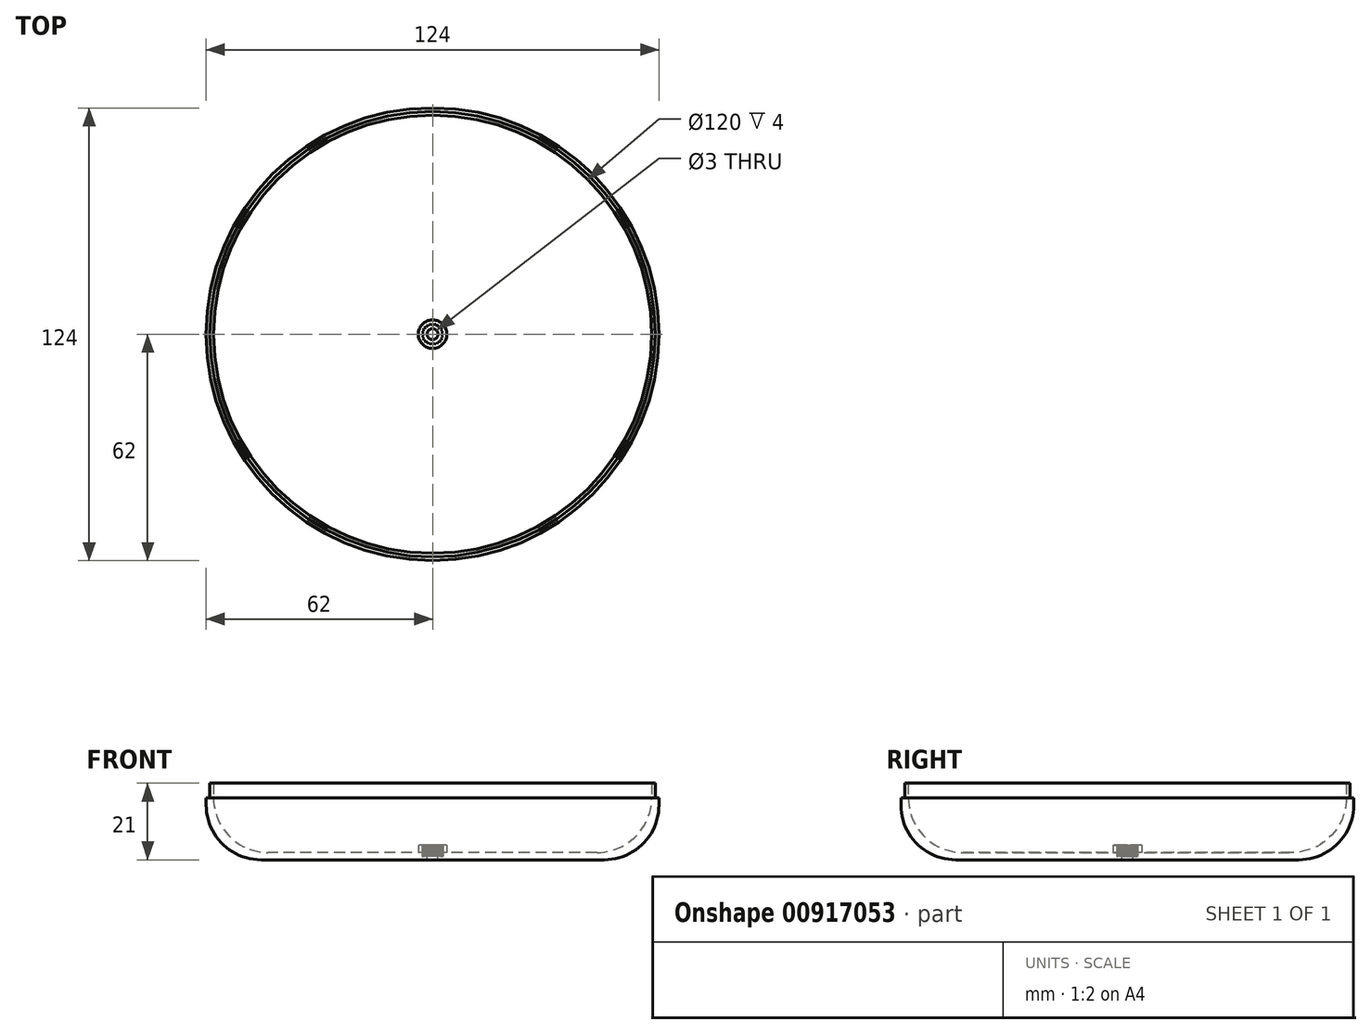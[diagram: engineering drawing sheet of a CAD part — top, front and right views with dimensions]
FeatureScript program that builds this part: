
annotation { "Feature Type Name" : "Feature", "Feature Type Description" : "" }
export const myFeature = defineFeature(function(context is Context, id is Id, definition is map)
    precondition{}
    {
        {
            var Q0;
            Q0=qCreatedBy(makeId("Top.planeOp"),FACE);
            var sketch = newSketch(context, id + "F0", { "sketchPlane" : qUnion([Q0])});
            skCircle(sketch, "E0", {"center": v(0, 0) * mm, "radius": 62 * mm});
            skSolve(sketch);
        }
        {
            var Q0;
            Q0=makeQuery(id+"F0.imprint","IMPRINT",FACE,{"disambiguationData":[TD([[makeQuery(id+"F0.imprint","IMPRINT",EDGE,{"derivedFrom":sQuery(id+"F0.wireOp",EDGE,"E0")}),1.0]])]});
            extrude(context, id + "F1", {"entities" : qUnion([Q0]), "oppositeDirection" : true, "depth" : 17 * mm, "offsetDistance" : 25 * mm});
        }
        {
            var Q0;
            Q0=makeQuery(id+"F1.opExtrude","CAP_FACE",FACE,{"disambiguationData":[OSD([sQuery(id+"F0.wireOp",EDGE,"E0")])],"isStart":true});
            var sketch = newSketch(context, id + "F2", { "sketchPlane" : qUnion([Q0])});
            skCircle(sketch, "E1", {"center": v(0, 0) * mm, "radius": 60 * mm});
            skSolve(sketch);
        }
        {
            var Q0;
            Q0=makeQuery(id+"F2.imprint","IMPRINT",FACE,{"disambiguationData":[TD([[makeQuery(id+"F2.imprint","IMPRINT",EDGE,{"derivedFrom":sQuery(id+"F2.wireOp",EDGE,"E1")}),1.0]])]});
            extrude(context, id + "F3", {"entities" : qUnion([Q0]), "operationType" : NewBodyOperationType.REMOVE, "oppositeDirection" : true, "depth" : 15 * mm, "offsetDistance" : 25 * mm});
        }
        {
            var Q0;
            Q0=makeQuery(id+"F3.boolean.opBoolean","COPY",EDGE,{"derivedFrom":makeQuery(id+"F3.opExtrude","CAP_EDGE",EDGE,{"disambiguationData":[OSD([sQuery(id+"F2.wireOp",EDGE,"E1")])],"isStart":false})});
            var Q1;
            Q1=makeQuery(id+"F1.opExtrude","CAP_EDGE",EDGE,{"disambiguationData":[OSD([sQuery(id+"F0.wireOp",EDGE,"E0")])],"isStart":false});
            fillet(context, id + "F4", {"entities" : qUnion([Q0, Q1]), "radius" : 15 * mm, "tangentPropagation" : true, "allowEdgeOverflow" : false});
        }
        {
            var Q0;
            Q0=makeQuery(id+"F1.opExtrude","CAP_FACE",FACE,{"disambiguationData":[OSD([sQuery(id+"F0.wireOp",EDGE,"E0")])],"isStart":true});
            var sketch = newSketch(context, id + "F5", { "sketchPlane" : qUnion([Q0])});
            skCircle(sketch, "E2", {"center": v(0, 0) * mm, "radius": 61 * mm});
            skSolve(sketch);
        }
        {
            var Q0;
            Q0=makeQuery(id+"F5.imprint","IMPRINT",FACE,{"disambiguationData":[TD([[makeQuery(id+"F5.imprint","IMPRINT",EDGE,{"derivedFrom":sQuery(id+"F5.wireOp",EDGE,"E2")}),1.0]])]});
            extrude(context, id + "F6", {"entities" : qUnion([Q0]), "operationType" : NewBodyOperationType.ADD, "depth" : 4 * mm, "offsetDistance" : 25 * mm});
        }
        {
            var Q0;
            Q0=makeQuery(id+"F3.boolean.opBoolean","COPY",FACE,{"derivedFrom":makeQuery(id+"F3.opExtrude","CAP_FACE",FACE,{"disambiguationData":[OSD([sQuery(id+"F2.wireOp",EDGE,"E1")])],"isStart":false})});
            var sketch = newSketch(context, id + "F7", { "sketchPlane" : qUnion([Q0])});
            skCircle(sketch, "E3", {"center": v(0, 0) * mm, "radius": 2.56 * mm});
            skPoint(sketch, "E4", {"position": v(2.56, 0) * mm});
            skPoint(sketch, "E5.1.0", {"position": v(2.47, 0.66) * mm});
            skCircle(sketch, "E6", {"center": v(0, 0) * mm, "radius": 2.9 * mm});
            skPoint(sketch, "E7", {"position": v(2.88, 0.38) * mm});
            skLineSegment(sketch, "E8", {"start": v(0, 0) * mm, "end": v(2.47, 0.66) * mm});
            skLineSegment(sketch, "E9", {"start": v(0, 0) * mm, "end": v(2.56, 0) * mm});
            skLineSegment(sketch, "E10", {"start": v(0, 0) * mm, "end": v(2.88, 0.38) * mm});
            skLineSegment(sketch, "E11", {"start": v(2.47, 0.66) * mm, "end": v(2.88, 0.38) * mm});
            skLineSegment(sketch, "E12", {"start": v(2.88, 0.38) * mm, "end": v(2.56, 0) * mm});
            skPoint(sketch, "E13.1.0", {"position": v(2.22, 1.28) * mm});
            skLineSegment(sketch, "E13.1.2", {"start": v(2.22, 1.28) * mm, "end": v(2.68, 1.1) * mm});
            skLineSegment(sketch, "E13.1.3", {"start": v(2.68, 1.1) * mm, "end": v(2.47, 0.66) * mm});
            skPoint(sketch, "E13.1.4", {"position": v(2.68, 1.1) * mm});
            skPoint(sketch, "E13.2.0", {"position": v(1.81, 1.81) * mm});
            skPoint(sketch, "E13.2.1", {"position": v(2.22, 1.28) * mm});
            skLineSegment(sketch, "E13.2.2", {"start": v(1.81, 1.81) * mm, "end": v(2.3, 1.77) * mm});
            skLineSegment(sketch, "E13.2.3", {"start": v(2.3, 1.77) * mm, "end": v(2.22, 1.28) * mm});
            skPoint(sketch, "E13.2.4", {"position": v(2.3, 1.77) * mm});
            skPoint(sketch, "E13.3.0", {"position": v(1.28, 2.22) * mm});
            skPoint(sketch, "E13.3.1", {"position": v(1.81, 1.81) * mm});
            skLineSegment(sketch, "E13.3.2", {"start": v(1.28, 2.22) * mm, "end": v(1.77, 2.3) * mm});
            skLineSegment(sketch, "E13.3.3", {"start": v(1.77, 2.3) * mm, "end": v(1.81, 1.81) * mm});
            skPoint(sketch, "E13.3.4", {"position": v(1.77, 2.3) * mm});
            skPoint(sketch, "E13.4.0", {"position": v(0.66, 2.47) * mm});
            skPoint(sketch, "E13.4.1", {"position": v(1.28, 2.22) * mm});
            skLineSegment(sketch, "E13.4.2", {"start": v(0.66, 2.47) * mm, "end": v(1.1, 2.68) * mm});
            skLineSegment(sketch, "E13.4.3", {"start": v(1.1, 2.68) * mm, "end": v(1.28, 2.22) * mm});
            skPoint(sketch, "E13.4.4", {"position": v(1.1, 2.68) * mm});
            skPoint(sketch, "E13.5.0", {"position": v(0, 2.56) * mm});
            skPoint(sketch, "E13.5.1", {"position": v(0.66, 2.47) * mm});
            skLineSegment(sketch, "E13.5.2", {"start": v(0, 2.56) * mm, "end": v(0.38, 2.88) * mm});
            skLineSegment(sketch, "E13.5.3", {"start": v(0.38, 2.88) * mm, "end": v(0.66, 2.47) * mm});
            skPoint(sketch, "E13.5.4", {"position": v(0.38, 2.88) * mm});
            skPoint(sketch, "E13.6.0", {"position": v(-0.66, 2.47) * mm});
            skPoint(sketch, "E13.6.1", {"position": v(0, 2.56) * mm});
            skLineSegment(sketch, "E13.6.2", {"start": v(-0.66, 2.47) * mm, "end": v(-0.38, 2.88) * mm});
            skLineSegment(sketch, "E13.6.3", {"start": v(-0.38, 2.88) * mm, "end": v(0, 2.56) * mm});
            skPoint(sketch, "E13.6.4", {"position": v(-0.38, 2.88) * mm});
            skPoint(sketch, "E13.7.0", {"position": v(-1.28, 2.22) * mm});
            skPoint(sketch, "E13.7.1", {"position": v(-0.66, 2.47) * mm});
            skLineSegment(sketch, "E13.7.2", {"start": v(-1.28, 2.22) * mm, "end": v(-1.1, 2.68) * mm});
            skLineSegment(sketch, "E13.7.3", {"start": v(-1.1, 2.68) * mm, "end": v(-0.66, 2.47) * mm});
            skPoint(sketch, "E13.7.4", {"position": v(-1.1, 2.68) * mm});
            skPoint(sketch, "E13.8.0", {"position": v(-1.81, 1.81) * mm});
            skPoint(sketch, "E13.8.1", {"position": v(-1.28, 2.22) * mm});
            skLineSegment(sketch, "E13.8.2", {"start": v(-1.81, 1.81) * mm, "end": v(-1.77, 2.3) * mm});
            skLineSegment(sketch, "E13.8.3", {"start": v(-1.77, 2.3) * mm, "end": v(-1.28, 2.22) * mm});
            skPoint(sketch, "E13.8.4", {"position": v(-1.77, 2.3) * mm});
            skPoint(sketch, "E13.9.0", {"position": v(-2.22, 1.28) * mm});
            skPoint(sketch, "E13.9.1", {"position": v(-1.81, 1.81) * mm});
            skLineSegment(sketch, "E13.9.2", {"start": v(-2.22, 1.28) * mm, "end": v(-2.3, 1.77) * mm});
            skLineSegment(sketch, "E13.9.3", {"start": v(-2.3, 1.77) * mm, "end": v(-1.81, 1.81) * mm});
            skPoint(sketch, "E13.9.4", {"position": v(-2.3, 1.77) * mm});
            skPoint(sketch, "E13.10.0", {"position": v(-2.47, 0.66) * mm});
            skPoint(sketch, "E13.10.1", {"position": v(-2.22, 1.28) * mm});
            skLineSegment(sketch, "E13.10.2", {"start": v(-2.47, 0.66) * mm, "end": v(-2.68, 1.1) * mm});
            skLineSegment(sketch, "E13.10.3", {"start": v(-2.68, 1.1) * mm, "end": v(-2.22, 1.28) * mm});
            skPoint(sketch, "E13.10.4", {"position": v(-2.68, 1.1) * mm});
            skPoint(sketch, "E13.11.0", {"position": v(-2.56, 0) * mm});
            skPoint(sketch, "E13.11.1", {"position": v(-2.47, 0.66) * mm});
            skLineSegment(sketch, "E13.11.2", {"start": v(-2.56, 0) * mm, "end": v(-2.88, 0.38) * mm});
            skLineSegment(sketch, "E13.11.3", {"start": v(-2.88, 0.38) * mm, "end": v(-2.47, 0.66) * mm});
            skPoint(sketch, "E13.11.4", {"position": v(-2.88, 0.38) * mm});
            skPoint(sketch, "E13.12.0", {"position": v(-2.47, -0.66) * mm});
            skPoint(sketch, "E13.12.1", {"position": v(-2.56, 0) * mm});
            skLineSegment(sketch, "E13.12.2", {"start": v(-2.47, -0.66) * mm, "end": v(-2.88, -0.38) * mm});
            skLineSegment(sketch, "E13.12.3", {"start": v(-2.88, -0.38) * mm, "end": v(-2.56, 0) * mm});
            skPoint(sketch, "E13.12.4", {"position": v(-2.88, -0.38) * mm});
            skPoint(sketch, "E13.13.0", {"position": v(-2.22, -1.28) * mm});
            skPoint(sketch, "E13.13.1", {"position": v(-2.47, -0.66) * mm});
            skLineSegment(sketch, "E13.13.2", {"start": v(-2.22, -1.28) * mm, "end": v(-2.68, -1.1) * mm});
            skLineSegment(sketch, "E13.13.3", {"start": v(-2.68, -1.1) * mm, "end": v(-2.47, -0.66) * mm});
            skPoint(sketch, "E13.13.4", {"position": v(-2.68, -1.1) * mm});
            skPoint(sketch, "E13.14.0", {"position": v(-1.81, -1.81) * mm});
            skPoint(sketch, "E13.14.1", {"position": v(-2.22, -1.28) * mm});
            skLineSegment(sketch, "E13.14.2", {"start": v(-1.81, -1.81) * mm, "end": v(-2.3, -1.77) * mm});
            skLineSegment(sketch, "E13.14.3", {"start": v(-2.3, -1.77) * mm, "end": v(-2.22, -1.28) * mm});
            skPoint(sketch, "E13.14.4", {"position": v(-2.3, -1.77) * mm});
            skPoint(sketch, "E13.15.0", {"position": v(-1.28, -2.22) * mm});
            skPoint(sketch, "E13.15.1", {"position": v(-1.81, -1.81) * mm});
            skLineSegment(sketch, "E13.15.2", {"start": v(-1.28, -2.22) * mm, "end": v(-1.77, -2.3) * mm});
            skLineSegment(sketch, "E13.15.3", {"start": v(-1.77, -2.3) * mm, "end": v(-1.81, -1.81) * mm});
            skPoint(sketch, "E13.15.4", {"position": v(-1.77, -2.3) * mm});
            skPoint(sketch, "E13.16.0", {"position": v(-0.66, -2.47) * mm});
            skPoint(sketch, "E13.16.1", {"position": v(-1.28, -2.22) * mm});
            skLineSegment(sketch, "E13.16.2", {"start": v(-0.66, -2.47) * mm, "end": v(-1.1, -2.68) * mm});
            skLineSegment(sketch, "E13.16.3", {"start": v(-1.1, -2.68) * mm, "end": v(-1.28, -2.22) * mm});
            skPoint(sketch, "E13.16.4", {"position": v(-1.1, -2.68) * mm});
            skPoint(sketch, "E13.17.0", {"position": v(0, -2.56) * mm});
            skPoint(sketch, "E13.17.1", {"position": v(-0.66, -2.47) * mm});
            skLineSegment(sketch, "E13.17.2", {"start": v(0, -2.56) * mm, "end": v(-0.38, -2.88) * mm});
            skLineSegment(sketch, "E13.17.3", {"start": v(-0.38, -2.88) * mm, "end": v(-0.66, -2.47) * mm});
            skPoint(sketch, "E13.17.4", {"position": v(-0.38, -2.88) * mm});
            skPoint(sketch, "E13.18.0", {"position": v(0.66, -2.47) * mm});
            skPoint(sketch, "E13.18.1", {"position": v(0, -2.56) * mm});
            skLineSegment(sketch, "E13.18.2", {"start": v(0.66, -2.47) * mm, "end": v(0.38, -2.88) * mm});
            skLineSegment(sketch, "E13.18.3", {"start": v(0.38, -2.88) * mm, "end": v(0, -2.56) * mm});
            skPoint(sketch, "E13.18.4", {"position": v(0.38, -2.88) * mm});
            skPoint(sketch, "E13.19.0", {"position": v(1.28, -2.22) * mm});
            skPoint(sketch, "E13.19.1", {"position": v(0.66, -2.47) * mm});
            skLineSegment(sketch, "E13.19.2", {"start": v(1.28, -2.22) * mm, "end": v(1.1, -2.68) * mm});
            skLineSegment(sketch, "E13.19.3", {"start": v(1.1, -2.68) * mm, "end": v(0.66, -2.47) * mm});
            skPoint(sketch, "E13.19.4", {"position": v(1.1, -2.68) * mm});
            skPoint(sketch, "E13.20.0", {"position": v(1.81, -1.81) * mm});
            skPoint(sketch, "E13.20.1", {"position": v(1.28, -2.22) * mm});
            skLineSegment(sketch, "E13.20.2", {"start": v(1.81, -1.81) * mm, "end": v(1.77, -2.3) * mm});
            skLineSegment(sketch, "E13.20.3", {"start": v(1.77, -2.3) * mm, "end": v(1.28, -2.22) * mm});
            skPoint(sketch, "E13.20.4", {"position": v(1.77, -2.3) * mm});
            skPoint(sketch, "E13.21.0", {"position": v(2.22, -1.28) * mm});
            skPoint(sketch, "E13.21.1", {"position": v(1.81, -1.81) * mm});
            skLineSegment(sketch, "E13.21.2", {"start": v(2.22, -1.28) * mm, "end": v(2.3, -1.77) * mm});
            skLineSegment(sketch, "E13.21.3", {"start": v(2.3, -1.77) * mm, "end": v(1.81, -1.81) * mm});
            skPoint(sketch, "E13.21.4", {"position": v(2.3, -1.77) * mm});
            skPoint(sketch, "E13.22.0", {"position": v(2.47, -0.66) * mm});
            skPoint(sketch, "E13.22.1", {"position": v(2.22, -1.28) * mm});
            skLineSegment(sketch, "E13.22.2", {"start": v(2.47, -0.66) * mm, "end": v(2.68, -1.1) * mm});
            skLineSegment(sketch, "E13.22.3", {"start": v(2.68, -1.1) * mm, "end": v(2.22, -1.28) * mm});
            skPoint(sketch, "E13.22.4", {"position": v(2.68, -1.1) * mm});
            skPoint(sketch, "E13.23.1", {"position": v(2.47, -0.66) * mm});
            skLineSegment(sketch, "E13.23.2", {"start": v(2.56, 0) * mm, "end": v(2.88, -0.38) * mm});
            skLineSegment(sketch, "E13.23.3", {"start": v(2.88, -0.38) * mm, "end": v(2.47, -0.66) * mm});
            skPoint(sketch, "E13.23.4", {"position": v(2.88, -0.38) * mm});
            skCircle(sketch, "E14", {"center": v(0, 0) * mm, "radius": 3.9 * mm});
            skSolve(sketch);
        }
        {
            var Q0;
            Q0=makeQuery(id+"F7.imprint","IMPRINT",FACE,{"disambiguationData":[TD([[makeQuery(id+"F7.imprint","IMPRINT",EDGE,{"derivedFrom":sQuery(id+"F7.wireOp",EDGE,"E14")}),1.0]])]});
            var Q1;
            {var subQ0=sQuery(id+"F7.wireOp",EDGE,"E13.9.2");Q1=makeQuery(id+"F7.imprint","IMPRINT",FACE,{"disambiguationData":[TD([[makeQuery(id+"F7.imprint","IMPRINT",EDGE,{"derivedFrom":subQ0}),1.0]])]});}
            var Q2;
            {var subQ0=sQuery(id+"F7.wireOp",EDGE,"E13.8.2");Q2=makeQuery(id+"F7.imprint","IMPRINT",FACE,{"disambiguationData":[TD([[makeQuery(id+"F7.imprint","IMPRINT",EDGE,{"derivedFrom":subQ0}),1.0]])]});}
            var Q3;
            {var subQ0=sQuery(id+"F7.wireOp",EDGE,"E13.7.2");Q3=makeQuery(id+"F7.imprint","IMPRINT",FACE,{"disambiguationData":[TD([[makeQuery(id+"F7.imprint","IMPRINT",EDGE,{"derivedFrom":subQ0}),1.0]])]});}
            var Q4;
            {var subQ0=sQuery(id+"F7.wireOp",EDGE,"E13.6.2");Q4=makeQuery(id+"F7.imprint","IMPRINT",FACE,{"disambiguationData":[TD([[makeQuery(id+"F7.imprint","IMPRINT",EDGE,{"derivedFrom":subQ0}),1.0]])]});}
            var Q5;
            {var subQ0=sQuery(id+"F7.wireOp",EDGE,"E13.5.2");Q5=makeQuery(id+"F7.imprint","IMPRINT",FACE,{"disambiguationData":[TD([[makeQuery(id+"F7.imprint","IMPRINT",EDGE,{"derivedFrom":subQ0}),1.0]])]});}
            var Q6;
            {var subQ0=sQuery(id+"F7.wireOp",EDGE,"E13.4.2");Q6=makeQuery(id+"F7.imprint","IMPRINT",FACE,{"disambiguationData":[TD([[makeQuery(id+"F7.imprint","IMPRINT",EDGE,{"derivedFrom":subQ0}),1.0]])]});}
            var Q7;
            {var subQ0=sQuery(id+"F7.wireOp",EDGE,"E13.3.2");Q7=makeQuery(id+"F7.imprint","IMPRINT",FACE,{"disambiguationData":[TD([[makeQuery(id+"F7.imprint","IMPRINT",EDGE,{"derivedFrom":subQ0}),1.0]])]});}
            var Q8;
            {var subQ0=sQuery(id+"F7.wireOp",EDGE,"E13.2.2");Q8=makeQuery(id+"F7.imprint","IMPRINT",FACE,{"disambiguationData":[TD([[makeQuery(id+"F7.imprint","IMPRINT",EDGE,{"derivedFrom":subQ0}),1.0]])]});}
            var Q9;
            {var subQ0=sQuery(id+"F7.wireOp",EDGE,"E13.1.2");Q9=makeQuery(id+"F7.imprint","IMPRINT",FACE,{"disambiguationData":[TD([[makeQuery(id+"F7.imprint","IMPRINT",EDGE,{"derivedFrom":subQ0}),1.0]])]});}
            var Q10;
            {var subQ0=sQuery(id+"F7.wireOp",EDGE,"E11");Q10=makeQuery(id+"F7.imprint","IMPRINT",FACE,{"disambiguationData":[TD([[makeQuery(id+"F7.imprint","IMPRINT",EDGE,{"derivedFrom":subQ0}),1.0]])]});}
            var Q11;
            {var subQ0=sQuery(id+"F7.wireOp",EDGE,"E12");Q11=makeQuery(id+"F7.imprint","IMPRINT",FACE,{"disambiguationData":[TD([[makeQuery(id+"F7.imprint","IMPRINT",EDGE,{"derivedFrom":subQ0}),1.0]])]});}
            var Q12;
            {var subQ0=sQuery(id+"F7.wireOp",EDGE,"E13.22.2");Q12=makeQuery(id+"F7.imprint","IMPRINT",FACE,{"disambiguationData":[TD([[makeQuery(id+"F7.imprint","IMPRINT",EDGE,{"derivedFrom":subQ0}),1.0]])]});}
            var Q13;
            {var subQ0=sQuery(id+"F7.wireOp",EDGE,"E13.21.2");Q13=makeQuery(id+"F7.imprint","IMPRINT",FACE,{"disambiguationData":[TD([[makeQuery(id+"F7.imprint","IMPRINT",EDGE,{"derivedFrom":subQ0}),1.0]])]});}
            var Q14;
            {var subQ0=sQuery(id+"F7.wireOp",EDGE,"E13.20.2");Q14=makeQuery(id+"F7.imprint","IMPRINT",FACE,{"disambiguationData":[TD([[makeQuery(id+"F7.imprint","IMPRINT",EDGE,{"derivedFrom":subQ0}),1.0]])]});}
            var Q15;
            {var subQ0=sQuery(id+"F7.wireOp",EDGE,"E13.19.2");Q15=makeQuery(id+"F7.imprint","IMPRINT",FACE,{"disambiguationData":[TD([[makeQuery(id+"F7.imprint","IMPRINT",EDGE,{"derivedFrom":subQ0}),1.0]])]});}
            var Q16;
            {var subQ0=sQuery(id+"F7.wireOp",EDGE,"E13.10.2");Q16=makeQuery(id+"F7.imprint","IMPRINT",FACE,{"disambiguationData":[TD([[makeQuery(id+"F7.imprint","IMPRINT",EDGE,{"derivedFrom":subQ0}),1.0]])]});}
            var Q17;
            {var subQ0=sQuery(id+"F7.wireOp",EDGE,"E13.11.2");Q17=makeQuery(id+"F7.imprint","IMPRINT",FACE,{"disambiguationData":[TD([[makeQuery(id+"F7.imprint","IMPRINT",EDGE,{"derivedFrom":subQ0}),1.0]])]});}
            var Q18;
            {var subQ0=sQuery(id+"F7.wireOp",EDGE,"E13.12.2");Q18=makeQuery(id+"F7.imprint","IMPRINT",FACE,{"disambiguationData":[TD([[makeQuery(id+"F7.imprint","IMPRINT",EDGE,{"derivedFrom":subQ0}),1.0]])]});}
            var Q19;
            {var subQ0=sQuery(id+"F7.wireOp",EDGE,"E13.13.2");Q19=makeQuery(id+"F7.imprint","IMPRINT",FACE,{"disambiguationData":[TD([[makeQuery(id+"F7.imprint","IMPRINT",EDGE,{"derivedFrom":subQ0}),1.0]])]});}
            var Q20;
            {var subQ0=sQuery(id+"F7.wireOp",EDGE,"E13.14.2");Q20=makeQuery(id+"F7.imprint","IMPRINT",FACE,{"disambiguationData":[TD([[makeQuery(id+"F7.imprint","IMPRINT",EDGE,{"derivedFrom":subQ0}),1.0]])]});}
            var Q21;
            {var subQ0=sQuery(id+"F7.wireOp",EDGE,"E13.15.2");Q21=makeQuery(id+"F7.imprint","IMPRINT",FACE,{"disambiguationData":[TD([[makeQuery(id+"F7.imprint","IMPRINT",EDGE,{"derivedFrom":subQ0}),1.0]])]});}
            var Q22;
            {var subQ0=sQuery(id+"F7.wireOp",EDGE,"E13.16.2");Q22=makeQuery(id+"F7.imprint","IMPRINT",FACE,{"disambiguationData":[TD([[makeQuery(id+"F7.imprint","IMPRINT",EDGE,{"derivedFrom":subQ0}),1.0]])]});}
            var Q23;
            {var subQ0=sQuery(id+"F7.wireOp",EDGE,"E13.17.2");Q23=makeQuery(id+"F7.imprint","IMPRINT",FACE,{"disambiguationData":[TD([[makeQuery(id+"F7.imprint","IMPRINT",EDGE,{"derivedFrom":subQ0}),1.0]])]});}
            var Q24;
            {var subQ0=sQuery(id+"F7.wireOp",EDGE,"E13.18.2");Q24=makeQuery(id+"F7.imprint","IMPRINT",FACE,{"disambiguationData":[TD([[makeQuery(id+"F7.imprint","IMPRINT",EDGE,{"derivedFrom":subQ0}),1.0]])]});}
            extrude(context, id + "F8", {"entities" : qUnion([Q0, Q1, Q2, Q3, Q4, Q5, Q6, Q7, Q8, Q9, Q10, Q11, Q12, Q13, Q14, Q15, Q16, Q17, Q18, Q19, Q20, Q21, Q22, Q23, Q24]), "operationType" : NewBodyOperationType.ADD, "depth" : 2 * mm, "offsetDistance" : 25 * mm});
        }
        {
            var Q0;
            Q0=makeQuery(id+"F8.boolean.opBoolean","SPLIT",FACE,{"disambiguationData":[TD([makeQuery(id+"F8.opExtrude","SWEPT_FACE",FACE,{"disambiguationData":[OSD([sQuery(id+"F7.wireOp",EDGE,"E11")])]})])],"derivedFrom":makeQuery(id+"F3.boolean.opBoolean","COPY",FACE,{"derivedFrom":makeQuery(id+"F3.opExtrude","CAP_FACE",FACE,{"disambiguationData":[OSD([sQuery(id+"F2.wireOp",EDGE,"E1")])],"isStart":false})})});
            extrude(context, id + "F9", {"entities" : qUnion([Q0]), "operationType" : NewBodyOperationType.REMOVE, "oppositeDirection" : true, "depth" : 1 * mm, "offsetDistance" : 25 * mm});
        }
        {
            var Q0;
            Q0=sQuery(id+"F7.wireOp",VERTEX,"E3.center");
            var Q1;
            Q1=makeQuery(id+"F1.opExtrude","SWEPT_BODY",BODY,{"disambiguationData":[OSD([sQuery(id+"F0.wireOp",EDGE,"E0")])]});
            hole(context, id + "F10", {"style" : HoleStyle.SIMPLE, "endStyle" : HoleEndStyle.THROUGH, "standardTappedOrClearance" : lookupTablePath({ "standard" : "ISO", "size" : "3", "type" : "Drilled" }), "standardBlindInLast" : lookupTablePath({ "standard" : "ISO", "size" : "3", "type" : "Drilled" }), "holeDiameter" : 3 * mm, "majorDiameter" : 6.35 * mm, "isTappedThrough" : true, "tappedDepth" : 12 * mm, "tapClearance" : 3, "locations" : qUnion([Q0]), "scope" : qUnion([Q1])});
        }
    });
